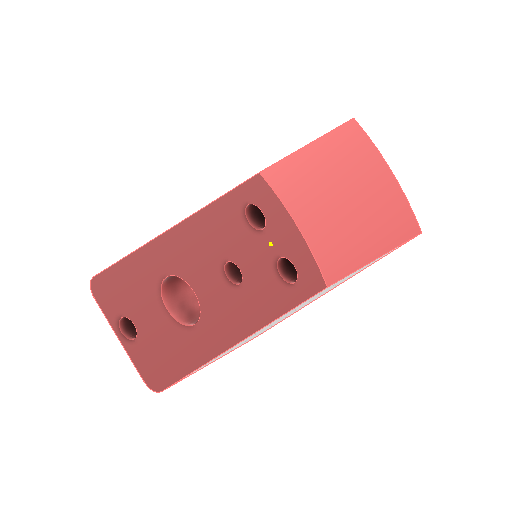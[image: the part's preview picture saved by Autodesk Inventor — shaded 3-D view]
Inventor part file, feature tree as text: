
AUTODESK INVENTOR PART (.ipt)
format: ipt  version: 2022 (Build 260153000, 153)  size: 134,144 bytes
history: native  units: mm
features: reference x5, other x5, sketch x3, extrude x1, fillet x1
ambient origin geometry x8: Origin, YZ Plane, XZ Plane, XY Plane, X Axis, Y Axis, Z Axis, Center Point
bodies: Volumenkörper1 (feature_tree)
feature tree (15):
  extrude  "Extrusion1"  Depth=6.2mm
  sketch  "Skizze2"  dims[d3=3.2mm]
  sketch  "Skizze3"  dims[d4=15.0mm d5=0.0mm d9=2.0mm]
  fillet  "Rundung1"  Radius=3.2mm
  sketch  "Skizze1"  dims[d0=30.0mm d1=6.2mm d2=3.2mm]
  reference  "Referenz1"
  reference  "Referenz2"
  reference  "Referenz3"
  reference  "Referenz4"
  reference  "Referenz5"
  other  "Assembly_Matchboxscope_injectionmolded_holo.iam"
  other  "IM_Matchboxscope_Laserholder:1"
  other  "00_laserpointer_red:2"
  other  "00_mk8_nozzle_0.4STEP:1"
  other  "IM_Lensholder:1"
